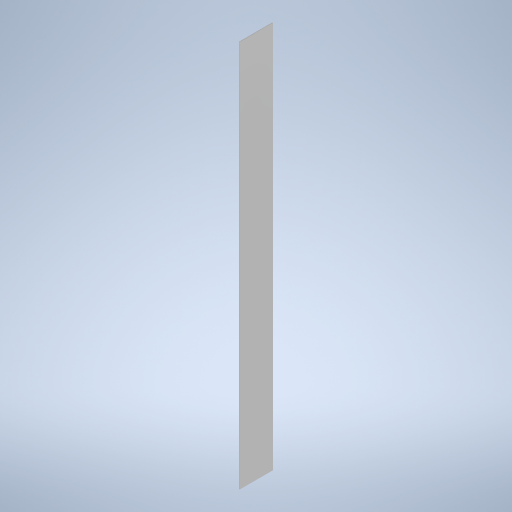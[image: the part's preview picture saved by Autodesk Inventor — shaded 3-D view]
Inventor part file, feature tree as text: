
AUTODESK INVENTOR PART (.ipt)
format: ipt  version: 2024 (Build 280153000, 153)  size: 230,912 bytes
history: native  units: mm
features: extrude x1, sketch x1
ambient origin geometry x8: Origin, YZ Plane, XZ Plane, XY Plane, X Axis, Y Axis, Z Axis, Center Point
bodies: Solid1 (feature_tree)
feature tree (2):
  extrude  "Extrusion1"  Depth=60.0mm
  sketch  "Sketch1"  dims[d0=1.0mm d1=60.0mm d2=700.0mm d3=0.0mm]
